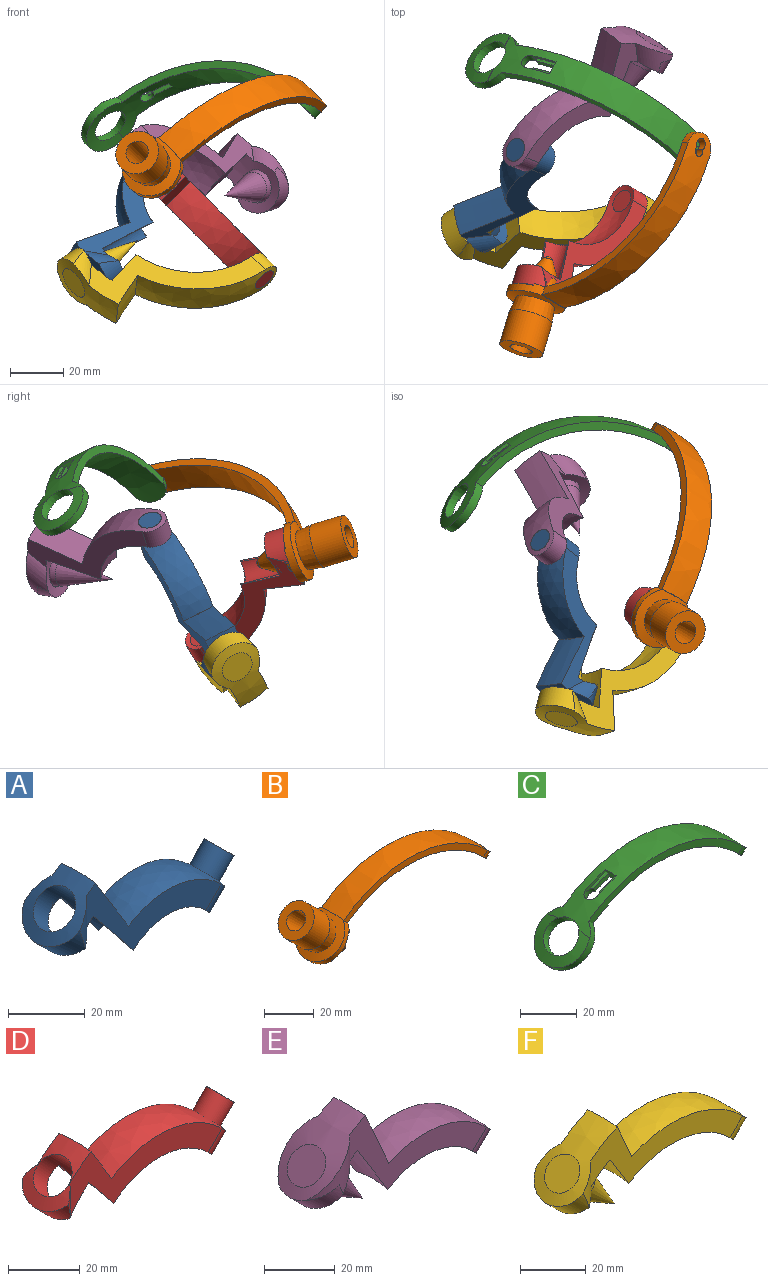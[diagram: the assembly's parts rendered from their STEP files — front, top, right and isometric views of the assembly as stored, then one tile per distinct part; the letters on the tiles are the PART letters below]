
ASSEMBLY  parts=6 mates=4
PART A: 17 faces, bbox 70.5x27x34.9 mm
  f0: sphere r=20.32mm, area 342.5mm2, adj f2,f3,f7,f8,f12,f13,f14
  f1: sphere r=27.94mm, area 480.5mm2, adj f2,f3,f4,f12,f13,f15
  f2: plane 49.43x28.99mm, normal (0,-1,0), area 406.8mm2, adj f0,f1,f4,f5,f6,f7,f9,f13
  f3: plane 49.43x28.99mm, normal (0,1,0), area 406.8mm2, adj f0,f1,f4,f5,f6,f8,f10,f13
  f4: cone r=43.08mm half-angle=58deg, axis (-1,0,0), area 292.3mm2, adj f1,f2,f3,f5,f12
  f5: sphere r=50.8mm, area 212mm2, adj f2,f3,f4,f9,f10,f11,f12
  f6: sphere r=43.18mm, area 82.5mm2, adj f2,f3,f7,f8,f9,f10,f11,f12
  f7: cone r=15.57mm half-angle=50deg, axis (-1,0,0), area 10.6mm2, adj f0,f2,f6,f12
  f8: cone r=15.57mm half-angle=50deg, axis (-1,0,0), area 10.6mm2, adj f0,f3,f6,f12
  f9: cylinder r=10.16mm len=14.19mm, axis (0,0,-1), area 59.8mm2, adj f2,f5,f6,f11
  f10: cylinder r=10.16mm len=14.19mm, axis (0,0,-1), area 59.8mm2, adj f3,f5,f6,f11
  f11: cylinder r=10.16mm len=20.03mm, axis (0.71,0,-0.71), area 195.6mm2, adj f5,f6,f9,f10
  f12: cylinder r=6.35mm len=30.97mm, axis (0.71,0,-0.71), area 668.7mm2, adj f0,f1,f4,f5,f6,f7,f8
  f13: cylinder r=6.35mm len=12.7mm, axis (-0.71,0,-0.71), area 157.7mm2, adj f0,f1,f2,f3
  f14: plane 8.89x6.29mm, normal (-0.71,0,-0.71), area 62.1mm2, adj f0
  f15: cylinder r=4.45mm len=11.73mm, axis (-0.71,0,-0.71), area 215mm2, adj f1,f16
  f16: plane 8.89x6.29mm, normal (0.71,0,0.71), area 62.1mm2, adj f15
PART B: 36 faces, bbox 112.8x26.4x33.2 mm
  f0: sphere r=60.07mm, area 1159.1mm2, adj f1,f2,f6,f9,f10,f11,f26,f27
  f1: cone r=6.43mm half-angle=6.9deg, axis (-0.71,0,0.71), area 134.6mm2, adj f0,f2,f3,f4,f5,f17,f21,f24
  f2: cone r=6.43mm half-angle=6.9deg, axis (-0.71,0,0.71), area 0.2mm2, adj f0,f1,f33
  f3: cone r=46.21mm half-angle=50deg, axis (-1,0,0), area 0.2mm2, adj f1,f5,f30
  f4: cone r=46.21mm half-angle=50deg, axis (-1,0,0), area 0.2mm2, adj f1,f5,f30
  f5: sphere r=60.32mm, area 100.4mm2, adj f1,f3,f4,f6,f29,f30,f32
  f6: cylinder r=11.43mm len=22.86mm, axis (0.71,0,-0.71), area 177.8mm2, adj f0,f5,f10,f11,f13,f29,f30,f32
  f7: cone r=3.13mm half-angle=3.1deg, axis (-0.71,0,0.71), area 530mm2, adj f14,f30
  f8: sphere r=63.25mm, area 1174.1mm2, adj f9,f10,f11,f12,f26,f27
  f9: cylinder r=2.28mm len=5mm, axis (0.73,0,0.68), area 34mm2, adj f0,f8,f27
  f10: plane 81.94x20.69mm, normal (0,1,0), area 277.1mm2, adj f0,f6,f8,f12,f13,f26
  f11: plane 81.94x20.69mm, normal (0,-1,0), area 277.1mm2, adj f0,f6,f8,f12,f13,f26
  f12: cone r=51.37mm half-angle=54deg, axis (-1,0,0), area 3.2mm2, adj f8,f10,f11,f13
  f13: sphere r=63.5mm, area 217.3mm2, adj f6,f10,f11,f12,f16
  f14: plane 16.76x11.85mm, normal (-0.71,0,0.71), area 160.1mm2, adj f7,f15
  f15: cylinder r=8.38mm len=20.83mm, axis (0.71,0,-0.71), area 668.9mm2, adj f14,f16
  f16: cone r=6.43mm half-angle=6.9deg, axis (-0.71,0,0.71), area 310.5mm2, adj f13,f15
  f17: cone r=1.8mm half-angle=30.4deg, axis (-0.71,0,0.71), area 236.6mm2, adj f1,f18,f22
  f18: sphere r=2.09mm, area 13.5mm2, adj f17
  f19: cone r=3.81mm half-angle=3.1deg, axis (-0.71,0,0.71), area 47.6mm2, adj f20,f23,f24,f25
  f20: sphere r=56.9mm, area 56.4mm2, adj f19,f21,f24,f25
  f21: torus R=6.4mm, axis (-0.71,0,0.71), area 23.1mm2, adj f1,f20,f24,f25
  f22: torus R=5.93mm, axis (-0.71,0,0.71), area 22mm2, adj f17,f23,f24,f25
  f23: sphere r=53.98mm, area 49.2mm2, adj f19,f22,f24,f25
  f24: plane 3.67x3.54mm, normal (-0.58,0.57,-0.58), area 8.7mm2, adj f1,f19,f20,f21,f22,f23
  f25: plane 3.67x3.54mm, normal (-0.58,-0.57,-0.58), area 8.7mm2, adj f1,f19,f20,f21,f22,f23
  f26: cylinder r=6.35mm len=12.7mm, axis (-0.71,0,-0.71), area 63.7mm2, adj f0,f8,f10,f11
  f27: cylinder r=2.03mm len=4.64mm, axis (-0.73,0,-0.68), area 28.5mm2, adj f0,f8,f9
  f28: plane 5.92x0.91mm, normal (0.71,0,0.71), area 7mm2, adj f1,f30,f31
  f29: plane 3.62x0.32mm, normal (0.71,0,0.71), area 0.8mm2, adj f5,f6,f30
  f30: plane 22.88x9.36mm, normal (0.71,0,-0.71), area 212.6mm2, adj f1,f3,f4,f5,f6,f7,f28,f29
  f31: plane 14.16x9.34mm, normal (-0.71,0,0.71), area 123.3mm2, adj f1,f28,f33,f35
  f32: plane 3.62x0.32mm, normal (0.71,0,0.71), area 0.8mm2, adj f5,f6,f30
  f33: plane 18.67x0.91mm, normal (-0.71,0,-0.71), area 11.2mm2, adj f0,f1,f2,f6,f30,f31
  f34: cone r=0mm half-angle=28.2deg, axis (-0.71,0,0.71), area 65.4mm2, adj f35
  f35: cone r=3.13mm half-angle=3.1deg, axis (-0.71,0,0.71), area 1mm2, adj f31,f34
PART C: 21 faces, bbox 96.8x31.8x29.9 mm
  f0: sphere r=56.9mm, area 1144.5mm2, adj f2,f3,f6,f7,f8,f9,f14,f15
  f1: sphere r=60.07mm, area 1134.9mm2, adj f6,f7,f11,f12,f14,f15,f16,f17
  f2: plane 7.97x4.53mm, normal (0,1,0), area 14.9mm2, adj f0,f4,f17,f20
  f3: plane 7.97x4.53mm, normal (0,-1,0), area 14.9mm2, adj f0,f5,f17,f20
  f4: cylinder r=58.8mm len=9.51mm, axis (0,-1,0), area 10.9mm2, adj f2,f17,f19,f20
  f5: cylinder r=58.8mm len=9.51mm, axis (0,-1,0), area 10.9mm2, adj f3,f17,f18,f20
  f6: plane 77.22x19.75mm, normal (0,1,0), area 261.2mm2, adj f0,f1,f14,f16
  f7: plane 77.22x19.75mm, normal (0,-1,0), area 261.2mm2, adj f0,f1,f14,f16
  f8: cone r=40.93mm half-angle=46deg, axis (-1,0,0), area 1.2mm2, adj f0,f10,f14,f15
  f9: cone r=40.93mm half-angle=46deg, axis (-1,0,0), area 1.2mm2, adj f0,f10,f14,f15
  f10: sphere r=57.15mm, area 135.1mm2, adj f8,f9,f14,f15
  f11: cone r=46.21mm half-angle=50deg, axis (-1,0,0), area 1.4mm2, adj f1,f13,f14,f15
  f12: cone r=46.21mm half-angle=50deg, axis (-1,0,0), area 1.4mm2, adj f1,f13,f14,f15
  f13: sphere r=60.32mm, area 166.4mm2, adj f11,f12,f14,f15
  f14: cylinder r=11.43mm len=22.86mm, axis (0.71,0,-0.71), area 191.3mm2, adj f0,f1,f6,f7,f8,f9,f10,f11
  f15: cone r=6.43mm half-angle=6.9deg, axis (-0.71,0,0.71), area 143.2mm2, adj f0,f1,f8,f9,f10,f11,f12,f13
  f16: cylinder r=6.35mm len=12.7mm, axis (-0.71,0,-0.71), area 63.7mm2, adj f0,f1,f6,f7
  f17: plane 5.6x3.07mm, normal (-0.96,0,-0.29), area 12.8mm2, adj f0,f1,f2,f3,f4,f5,f18,f19
  f18: plane 10.08x5.01mm, normal (0,-1,0), area 12.5mm2, adj f1,f5,f17,f20
  f19: plane 10.08x5.01mm, normal (0,1,0), area 12.5mm2, adj f1,f4,f17,f20
  f20: cylinder r=2.79mm len=6.02mm, axis (0.45,0,-0.89), area 38.7mm2, adj f0,f1,f2,f3,f4,f5,f18,f19
PART D: 17 faces, bbox 76.4x24.1x29.6 mm
  f0: sphere r=27.94mm, area 496.7mm2, adj f2,f3,f4,f10,f12,f13,f14
  f1: sphere r=35.56mm, area 610mm2, adj f2,f7,f10,f13,f15
  f2: plane 60.41x23.79mm, normal (0,-1,0), area 512mm2, adj f0,f1,f3,f5,f6,f7,f8,f13
  f3: cone r=21.4mm half-angle=50deg, axis (-1,0,0), area 11.8mm2, adj f0,f2,f6,f12
  f4: cone r=21.4mm half-angle=50deg, axis (-1,0,0), area 11.8mm2, adj f0,f6,f10,f12
  f5: sphere r=50.8mm, area 173.2mm2, adj f2,f7,f8,f9,f10,f11,f12
  f6: sphere r=43.18mm, area 65.2mm2, adj f2,f3,f4,f8,f9,f10,f11,f12
  f7: cone r=43.08mm half-angle=58deg, axis (-1,0,0), area 198.8mm2, adj f1,f2,f5,f10
  f8: cylinder r=10.16mm len=12.04mm, axis (0,0,-1), area 28.3mm2, adj f2,f5,f6,f11
  f9: cylinder r=10.16mm len=12.04mm, axis (0,0,-1), area 28.3mm2, adj f5,f6,f10,f11
  f10: plane 60.41x23.79mm, normal (0,1,0), area 512mm2, adj f0,f1,f4,f5,f6,f7,f9,f13
  f11: cylinder r=10.29mm len=18.14mm, axis (0.71,0,-0.71), area 141.2mm2, adj f5,f6,f8,f9
  f12: cylinder r=6.22mm len=25.19mm, axis (0.71,0,-0.71), area 517.4mm2, adj f0,f3,f4,f5,f6
  f13: cylinder r=6.35mm len=12.7mm, axis (-0.71,0,-0.71), area 155.2mm2, adj f0,f1,f2,f10
  f14: plane 8.89x6.29mm, normal (-0.71,0,-0.71), area 62.1mm2, adj f0
  f15: cylinder r=4.45mm len=11.71mm, axis (-0.71,0,-0.71), area 214.2mm2, adj f1,f16
  f16: plane 8.89x6.29mm, normal (0.71,0,0.71), area 62.1mm2, adj f15
PART E: 18 faces, bbox 78.3x26.2x40.6 mm
  f0: sphere r=27.94mm, area 480.5mm2, adj f1,f13,f14,f15,f16,f17
  f1: cylinder r=4.45mm len=11.73mm, axis (-0.71,0,-0.71), area 215mm2, adj f0,f2
  f2: sphere r=35.56mm, area 546.5mm2, adj f1,f3,f13,f16,f17
  f3: cone r=53.37mm half-angle=66deg, axis (-1,0,0), area 303.9mm2, adj f2,f4,f13,f16
  f4: sphere r=58.42mm, area 379mm2, adj f3,f5,f6,f11,f12,f13,f16
  f5: plane 12.7x8.98mm, normal (-0.71,0,0.71), area 126.7mm2, adj f4
  f6: cylinder r=10.16mm len=16.74mm, axis (0,0,-1), area 107.5mm2, adj f4,f7,f11,f13
  f7: sphere r=50.8mm, area 205mm2, adj f6,f8,f11,f12,f13,f15,f16
  f8: cylinder r=6.35mm len=12.7mm, axis (0.71,0,-0.71), area 100.4mm2, adj f7,f9
  f9: revolved ~12.7x11.97mm, area 189.1mm2, adj f8,f10
  f10: cone r=5.72mm half-angle=14.7deg, axis (-0.71,0,0.71), area 404.3mm2, adj f9
  f11: cylinder r=10.16mm len=20.32mm, axis (0.71,0,-0.71), area 201.7mm2, adj f4,f6,f7,f12
  f12: cylinder r=10.16mm len=16.74mm, axis (0,0,-1), area 107.5mm2, adj f4,f7,f11,f16
  f13: plane 56.12x34.96mm, normal (0,-1,0), area 491.5mm2, adj f0,f2,f3,f4,f6,f7,f15,f17
  f14: cylinder r=6.35mm len=2.01mm, axis (0.71,0,-0.71), area 0mm2, adj f0,f15
  f15: cone r=43.08mm half-angle=58deg, axis (-1,0,0), area 310.9mm2, adj f0,f7,f13,f14,f16
  f16: plane 56.12x34.96mm, normal (0,1,0), area 491.5mm2, adj f0,f2,f3,f4,f7,f12,f15,f17
  f17: cylinder r=6.35mm len=12.7mm, axis (-0.71,0,-0.71), area 155.2mm2, adj f0,f2,f13,f16
PART F: 17 faces, bbox 83.1x27x35.2 mm
  f0: sphere r=35.56mm, area 610mm2, adj f2,f6,f8,f15,f16
  f1: sphere r=43.18mm, area 662.7mm2, adj f2,f7,f8,f15,f16
  f2: plane 65.87x28.67mm, normal (0,-1,0), area 575.3mm2, adj f0,f1,f3,f4,f6,f7,f9,f15
  f3: sphere r=58.42mm, area 342.2mm2, adj f2,f5,f7,f8,f9,f10,f12
  f4: sphere r=50.8mm, area 173.2mm2, adj f2,f5,f6,f8,f9,f10,f11
  f5: cylinder r=10.16mm len=14.41mm, axis (0,0,-1), area 64.5mm2, adj f3,f4,f8,f10
  f6: cone r=43.08mm half-angle=58deg, axis (-1,0,0), area 198.8mm2, adj f0,f2,f4,f8
  f7: cone r=53.37mm half-angle=66deg, axis (-1,0,0), area 197.2mm2, adj f1,f2,f3,f8
  f8: plane 65.87x28.67mm, normal (0,1,0), area 575.3mm2, adj f0,f1,f3,f4,f5,f6,f7,f15
  f9: cylinder r=10.16mm len=14.41mm, axis (0,0,-1), area 64.5mm2, adj f2,f3,f4,f10
  f10: cylinder r=10.29mm len=20.19mm, axis (0.71,0,-0.71), area 196.2mm2, adj f3,f4,f5,f9
  f11: cylinder r=6.22mm len=12.45mm, axis (0.71,0,-0.71), area 96.5mm2, adj f4,f14
  f12: plane 12.45x8.8mm, normal (-0.71,0,0.71), area 121.7mm2, adj f3
  f13: cone r=5.62mm half-angle=14.5deg, axis (-0.71,0,0.71), area 397.3mm2, adj f14
  f14: revolved ~12.45x11.74mm, area 181.9mm2, adj f11,f13
  f15: cylinder r=6.35mm len=12.7mm, axis (-0.71,0,-0.71), area 154mm2, adj f0,f1,f2,f8
  f16: cylinder r=4.45mm len=11.71mm, axis (-0.71,0,-0.71), area 214.2mm2, adj f0,f1
PLACE A rot(axis=(-0.16,-0.93,0.33),86.2deg) t=(1.6,-6.56,-21.01)mm
PLACE B rot(axis=(0.71,0,0.71),67.1deg) t=(4.22,2.17,-23.61)mm
PLACE C rot(axis=(-0.71,0,-0.71),35.3deg) t=(4.22,2.17,-23.61)mm fixed
PLACE D rot(axis=(0.86,0.48,-0.17),107.8deg) t=(1.62,-6.55,-21)mm
PLACE E rot(axis=(-0.1,-0.44,-0.89),144.5deg) t=(1.6,-6.56,-21.01)mm
PLACE F rot(axis=(1,0.03,-0.05),145.2deg) t=(1.62,-6.55,-21)mm
MATE revolute D.f11 <-> B.f22  axis (0.28,0.92,-0.28) through (-12.27,-52.99,-7.11)mm
MATE revolute A.f15 <-> E.f1  axis (0.63,-0.24,-0.74) through (-15.72,0.09,-0.59)mm
MATE revolute F.f10 <-> A.f11  axis (0.75,0.42,0.5) through (-36.44,-27.73,-46.39)mm
MATE revolute D.f15 <-> F.f16  axis (-0.65,0.39,0.65) through (24.59,-20.3,-43.97)mm
